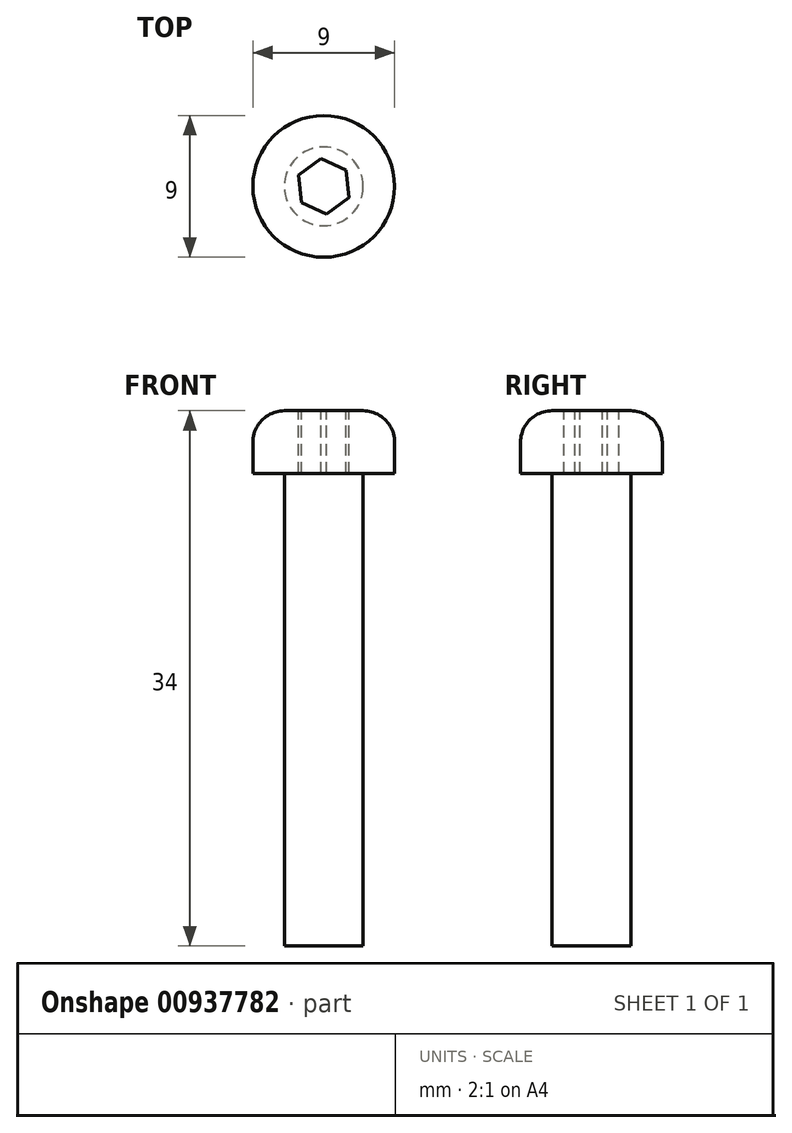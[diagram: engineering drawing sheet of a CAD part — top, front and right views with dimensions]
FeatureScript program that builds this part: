
annotation { "Feature Type Name" : "Feature", "Feature Type Description" : "" }
export const myFeature = defineFeature(function(context is Context, id is Id, definition is map)
    precondition{}
    {
        {
            var Q0;
            Q0=qCreatedBy(makeId("Top.planeOp"),FACE);
            var sketch = newSketch(context, id + "F0", { "sketchPlane" : qUnion([Q0])});
            skCircle(sketch, "E0", {"center": v(0, 0) * mm, "radius": 2.5 * mm});
            skSolve(sketch);
        }
        {
            var Q0;
            Q0=qSketchRegion(id+"F0",true);
            extrude(context, id + "F1", {"entities" : qUnion([Q0]), "depth" : 30 * mm, "offsetDistance" : 25 * mm});
        }
        {
            var Q0;
            Q0=makeQuery(id+"F1.opExtrude","CAP_FACE",FACE,{"disambiguationData":[OSD([sQuery(id+"F0.wireOp",EDGE,"E0")])],"isStart":false});
            var sketch = newSketch(context, id + "F2", { "sketchPlane" : qUnion([Q0])});
            skCircle(sketch, "E1", {"center": v(0, 0) * mm, "radius": 4.5 * mm});
            skSolve(sketch);
        }
        {
            var Q0;
            Q0=qSketchRegion(id+"F2",true);
            extrude(context, id + "F3", {"entities" : qUnion([Q0]), "operationType" : NewBodyOperationType.ADD, "depth" : 4 * mm, "offsetDistance" : 25 * mm});
        }
        {
            var Q0;
            Q0=makeQuery(id+"F3.opExtrude","CAP_EDGE",EDGE,{"disambiguationData":[OSD([sQuery(id+"F2.wireOp",EDGE,"E1")])],"isStart":false});
            fillet(context, id + "F4", {"entities" : qUnion([Q0]), "radius" : 2 * mm, "tangentPropagation" : true, "allowEdgeOverflow" : false});
        }
        {
            var Q0;
            Q0=makeQuery(id+"F3.opExtrude","CAP_FACE",FACE,{"disambiguationData":[OSD([sQuery(id+"F2.wireOp",EDGE,"E1")])],"isStart":false});
            var sketch = newSketch(context, id + "F5", { "sketchPlane" : qUnion([Q0])});
            skCircle(sketch, "E2.cCircle", {"center": v(0, 0) * mm, "radius": 1.52 * mm, "construction": true});
            skLineSegment(sketch, "E2.0", {"start": v(-1.6, 0.71) * mm, "end": v(-0.19, 1.75) * mm});
            skLineSegment(sketch, "E2.1", {"start": v(-0.19, 1.75) * mm, "end": v(1.42, 1.03) * mm});
            skLineSegment(sketch, "E2.2", {"start": v(1.42, 1.03) * mm, "end": v(1.6, -0.71) * mm});
            skLineSegment(sketch, "E2.3", {"start": v(1.6, -0.71) * mm, "end": v(0.19, -1.75) * mm});
            skLineSegment(sketch, "E2.4", {"start": v(0.19, -1.75) * mm, "end": v(-1.42, -1.03) * mm});
            skLineSegment(sketch, "E2.5", {"start": v(-1.42, -1.03) * mm, "end": v(-1.6, 0.71) * mm});
            skPoint(sketch, "E2.0.midPoint", {"position": v(-0.9, 1.23) * mm});
            skSolve(sketch);
        }
        {
            var Q0;
            Q0=qSketchRegion(id+"F5",true);
            extrude(context, id + "F6", {"entities" : qUnion([Q0]), "operationType" : NewBodyOperationType.REMOVE, "oppositeDirection" : true, "depth" : 4 * mm, "offsetDistance" : 25 * mm});
        }
    });
